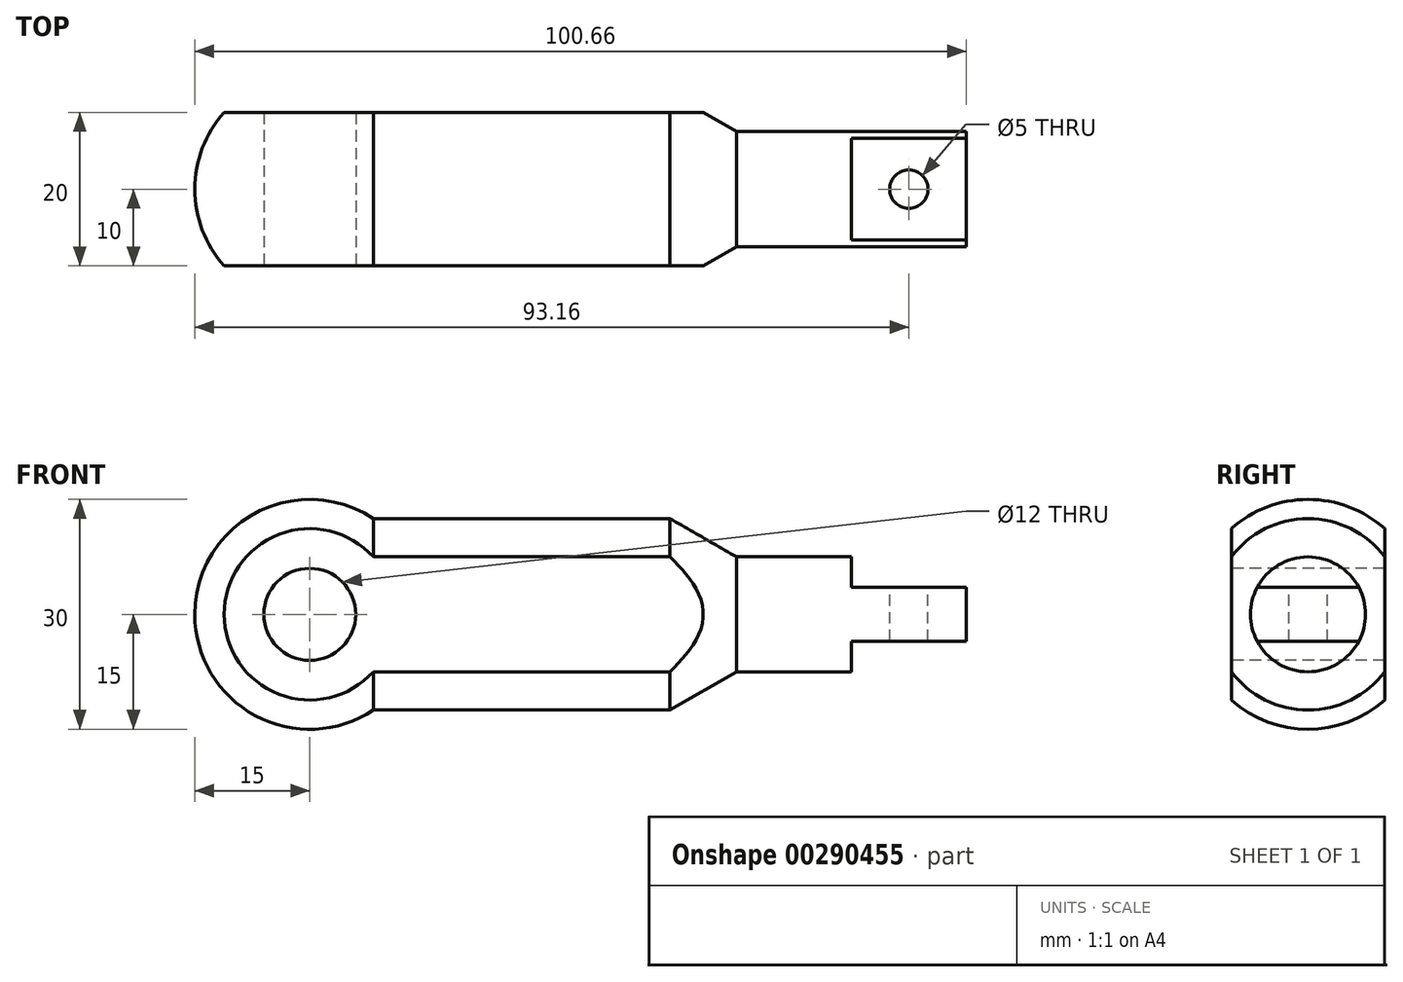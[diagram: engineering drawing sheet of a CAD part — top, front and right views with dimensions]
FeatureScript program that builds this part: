
annotation { "Feature Type Name" : "Feature", "Feature Type Description" : "" }
export const myFeature = defineFeature(function(context is Context, id is Id, definition is map)
    precondition{}
    {
        {
            var Q0;
            Q0=qCreatedBy(makeId("Front.planeOp"),FACE);
            var sketch = newSketch(context, id + "F0", { "sketchPlane" : qUnion([Q0])});
            skLineSegment(sketch, "E0", {"start": v(0, 0) * mm, "end": v(101.46, 0) * mm, "construction": true});
            skArc(sketch, "E1", {"start": v(-15, 0) * mm, "mid": v(-7.1, 13.22) * mm, "end": v(8.3, 12.5) * mm});
            skLineSegment(sketch, "E2", {"start": v(8.3, 12.5) * mm, "end": v(47, 12.5) * mm});
            skLineSegment(sketch, "E3", {"start": v(47, 12.5) * mm, "end": v(55.66, 7.5) * mm});
            skLineSegment(sketch, "E4", {"start": v(55.66, 7.5) * mm, "end": v(85.66, 7.5) * mm});
            skLineSegment(sketch, "E5", {"start": v(85.66, 7.5) * mm, "end": v(85.66, 0) * mm});
            skLineSegment(sketch, "E6", {"start": v(85.66, 0) * mm, "end": v(-15, 0) * mm});
            skSolve(sketch);
        }
        {
            var Q0;
            Q0 = qSketchRegion(id + "F0", true);
            var Q1;
            Q1=sQuery(id+"F0.wireOp",EDGE,"E0");
            revolve(context, id + "F1", {"entities" : qUnion([Q0]), "axis" : qUnion([Q1]), "revolveType" : RevolveType.FULL});
        }
        {
            var Q0;
            Q0=qCreatedBy(makeId("Front.planeOp"),FACE);
            var sketch = newSketch(context, id + "F2", { "sketchPlane" : qUnion([Q0])});
            skLineSegment(sketch, "E7.top", {"start": v(85.66, 3.5) * mm, "end": v(70.66, 3.5) * mm});
            skLineSegment(sketch, "E7.right", {"start": v(70.66, 7.5) * mm, "end": v(70.66, 3.5) * mm});
            skLineSegment(sketch, "E8", {"start": v(70.66, 7.5) * mm, "end": v(85.66, 7.5) * mm});
            skLineSegment(sketch, "E9", {"start": v(85.66, 7.5) * mm, "end": v(85.66, 3.5) * mm});
            skLineSegment(sketch, "E10", {"start": v(70.5, 0) * mm, "end": v(88.18, 0) * mm, "construction": true});
            skLineSegment(sketch, "E11.MirrorCS", {"start": v(85.66, -3.5) * mm, "end": v(70.66, -3.5) * mm});
            skLineSegment(sketch, "E12.MirrorCS", {"start": v(70.66, -7.5) * mm, "end": v(70.66, -3.5) * mm});
            skLineSegment(sketch, "E13.MirrorCS", {"start": v(85.66, -7.5) * mm, "end": v(85.66, -3.5) * mm});
            skLineSegment(sketch, "E14.MirrorCS", {"start": v(70.66, -7.5) * mm, "end": v(85.66, -7.5) * mm});
            skSolve(sketch);
        }
        {
            var Q0;
            Q0 = qSketchRegion(id + "F2", true);
            extrude(context, id + "F3", {"entities" : qUnion([Q0]), "operationType" : NewBodyOperationType.REMOVE, "endBound" : BoundingType.THROUGH_ALL, "oppositeDirection" : true, "depth" : 25 * mm, "hasSecondDirection" : true, "secondDirectionBound" : SecondDirectionBoundingType.THROUGH_ALL, "secondDirectionOppositeDirection" : false, "secondDirectionDepth" : 25 * mm});
        }
        {
            var Q0;
            Q0=makeQuery(id+"F1.opRevolve","SWEPT_FACE",FACE,{"disambiguationData":[OSD([sQuery(id+"F0.wireOp",EDGE,"E5")])]});
            var sketch = newSketch(context, id + "F4", { "sketchPlane" : qUnion([Q0])});
            skLineSegment(sketch, "E15", {"start": v(-10, 11.18) * mm, "end": v(-10, -11.18) * mm});
            skLineSegment(sketch, "E16", {"start": v(10, 11.18) * mm, "end": v(10, -11.18) * mm});
            skLineSegment(sketch, "E17", {"start": v(0, 0) * mm, "end": v(0, 29.82) * mm, "construction": true});
            skArc(sketch, "E18", {"start": v(10, -11.18) * mm, "mid": v(15, 0) * mm, "end": v(10, 11.18) * mm});
            skPoint(sketch, "E19.orphan", {"position": v(-10, 24.03) * mm});
            skPoint(sketch, "E20.orphan", {"position": v(10, 24) * mm});
            skArc(sketch, "E21.trimOffspring", {"start": v(-10, 11.18) * mm, "mid": v(-15, 0) * mm, "end": v(-10, -11.18) * mm});
            skSolve(sketch);
        }
        {
            var Q0;
            Q0=makeQuery(id+"F4.imprint","IMPRINT",FACE,{"disambiguationData":[TD([[makeQuery(id+"F4.imprint","IMPRINT",EDGE,{"derivedFrom":sQuery(id+"F4.wireOp",EDGE,"E16")}),1.0]])]});
            var Q1;
            Q1=makeQuery(id+"F4.imprint","IMPRINT",FACE,{"disambiguationData":[TD([[makeQuery(id+"F4.imprint","IMPRINT",EDGE,{"derivedFrom":sQuery(id+"F4.wireOp",EDGE,"E15")}),-1.0]])]});
            extrude(context, id + "F5", {"entities" : qUnion([Q0, Q1]), "operationType" : NewBodyOperationType.REMOVE, "endBound" : BoundingType.THROUGH_ALL, "oppositeDirection" : true, "depth" : 25 * mm});
        }
        {
            var Q0;
            Q0=makeQuery(id+"F5.boolean.opBoolean","COPY",FACE,{"derivedFrom":makeQuery(id+"F5.opExtrude","SWEPT_FACE",FACE,{"disambiguationData":[OSD([sQuery(id+"F4.wireOp",EDGE,"E15")])]})});
            var sketch = newSketch(context, id + "F6", { "sketchPlane" : qUnion([Q0])});
            skCircle(sketch, "E22", {"center": v(0, 0) * mm, "radius": 6 * mm});
            skSolve(sketch);
        }
        {
            var Q0;
            Q0=makeQuery(id+"F6.imprint","IMPRINT",FACE,{"disambiguationData":[TD([[makeQuery(id+"F6.imprint","IMPRINT",EDGE,{"derivedFrom":sQuery(id+"F6.wireOp",EDGE,"E22")}),1.0]])]});
            extrude(context, id + "F7", {"entities" : qUnion([Q0]), "operationType" : NewBodyOperationType.REMOVE, "endBound" : BoundingType.THROUGH_ALL, "oppositeDirection" : true, "depth" : 25 * mm});
        }
        {
            var Q0;
            Q0=makeQuery(id+"F3.boolean.opBoolean","COPY",FACE,{"derivedFrom":makeQuery(id+"F3.opExtrude","SWEPT_FACE",FACE,{"disambiguationData":[OSD([sQuery(id+"F2.wireOp",EDGE,"E7.top")])]})});
            var sketch = newSketch(context, id + "F8", { "sketchPlane" : qUnion([Q0])});
            skCircle(sketch, "E23", {"center": v(78.16, 0) * mm, "radius": 2.5 * mm});
            skSolve(sketch);
        }
        {
            var Q0;
            Q0=makeQuery(id+"F8.imprint","IMPRINT",FACE,{"disambiguationData":[TD([[makeQuery(id+"F8.imprint","IMPRINT",EDGE,{"derivedFrom":sQuery(id+"F8.wireOp",EDGE,"E23")}),1.0]])]});
            extrude(context, id + "F9", {"entities" : qUnion([Q0]), "operationType" : NewBodyOperationType.REMOVE, "endBound" : BoundingType.THROUGH_ALL, "oppositeDirection" : true, "depth" : 25 * mm});
        }
    });
